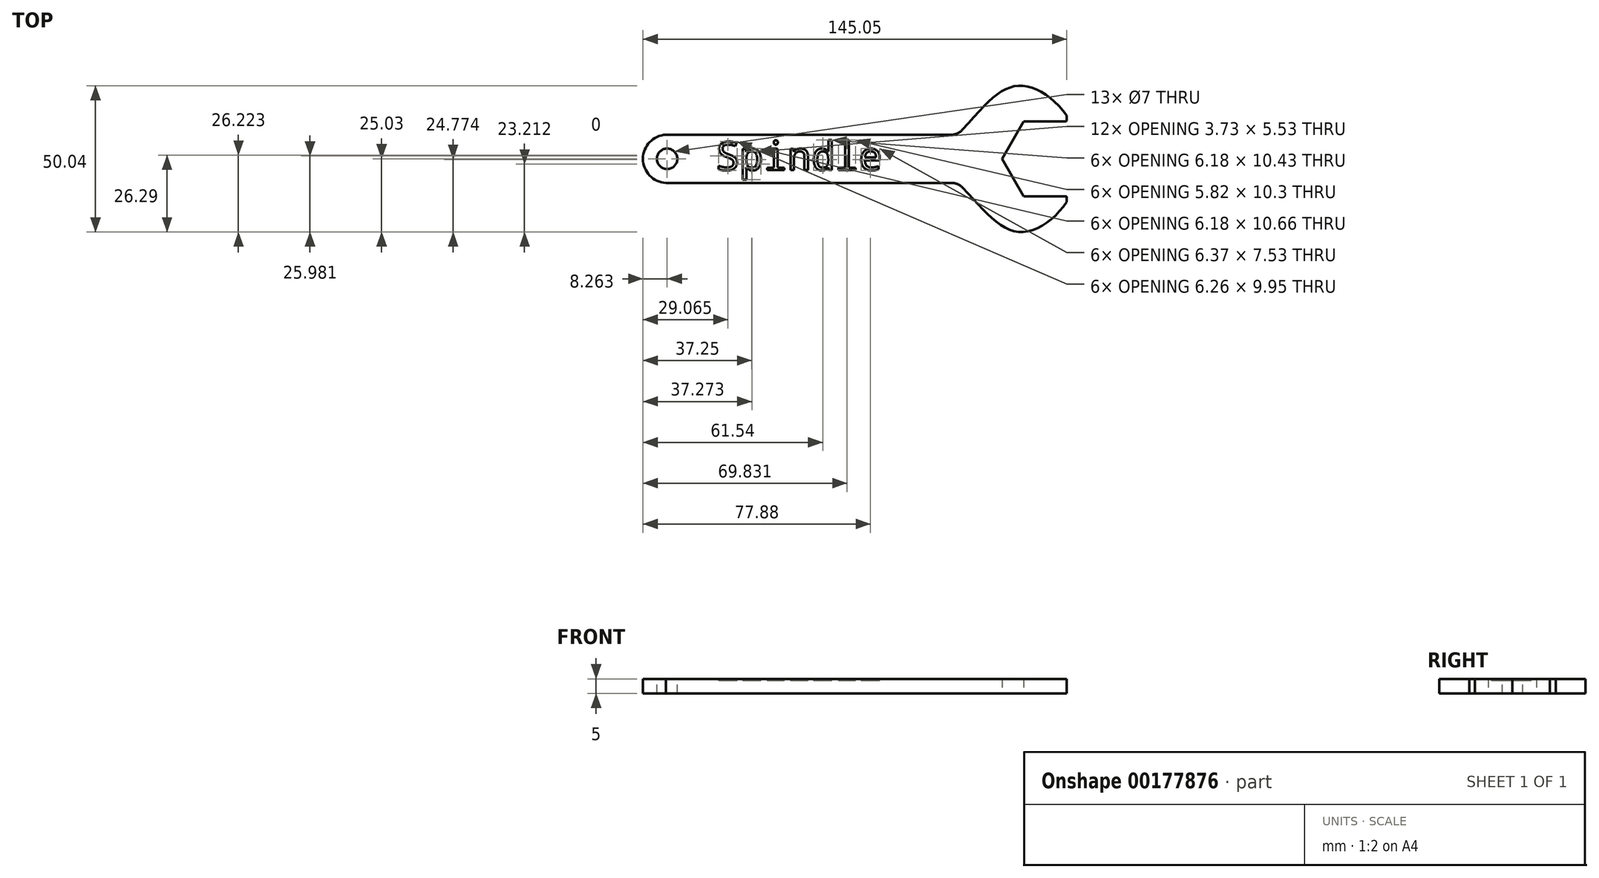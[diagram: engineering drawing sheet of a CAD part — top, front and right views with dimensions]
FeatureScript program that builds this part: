
annotation { "Feature Type Name" : "Feature", "Feature Type Description" : "" }
export const myFeature = defineFeature(function(context is Context, id is Id, definition is map)
    precondition{}
    {
        {
            var Q0;
            Q0=qCreatedBy(makeId("Top.planeOp"),FACE);
            var sketch = newSketch(context, id + "F0", { "sketchPlane" : qUnion([Q0])});
            skCircle(sketch, "E0.cCircle", {"center": v(0, 0) * mm, "radius": 12.8 * mm, "construction": true});
            skLineSegment(sketch, "E0.0", {"start": v(-7.4, 12.8) * mm, "end": v(7.4, 12.8) * mm});
            skLineSegment(sketch, "E0.1", {"start": v(7.4, 12.8) * mm, "end": v(14.78, 0) * mm});
            skLineSegment(sketch, "E0.2", {"start": v(14.78, 0) * mm, "end": v(7.4, -12.8) * mm});
            skLineSegment(sketch, "E0.3", {"start": v(7.4, -12.8) * mm, "end": v(-7.4, -12.8) * mm});
            skLineSegment(sketch, "E0.4", {"start": v(-7.4, -12.8) * mm, "end": v(-14.78, 0) * mm});
            skLineSegment(sketch, "E0.5", {"start": v(-14.78, 0) * mm, "end": v(-7.4, 12.8) * mm});
            skPoint(sketch, "E0.0.midPoint", {"position": v(0, 12.8) * mm});
            skLineSegment(sketch, "E1.bottom", {"start": v(-29.78, 8.25) * mm, "end": v(-29.78, 8.25) * mm});
            skLineSegment(sketch, "E1.top", {"start": v(-29.78, -8.25) * mm, "end": v(-29.78, -8.25) * mm});
            skLineSegment(sketch, "E1.left", {"start": v(-29.78, 8.25) * mm, "end": v(-29.78, -8.25) * mm});
            skLineSegment(sketch, "E1.right", {"start": v(-29.78, 8.25) * mm, "end": v(-29.78, -8.25) * mm});
            skLineSegment(sketch, "E2.bottom", {"start": v(-129.78, 8.25) * mm, "end": v(-29.78, 8.25) * mm});
            skLineSegment(sketch, "E2.top", {"start": v(-129.78, -8.25) * mm, "end": v(-29.78, -8.25) * mm});
            skLineSegment(sketch, "E2.left", {"start": v(-129.78, 8.25) * mm, "end": v(-129.78, -8.25) * mm});
            skCircle(sketch, "E3", {"center": v(-129.4, 0) * mm, "radius": 8.26 * mm});
            skPoint(sketch, "E3.third.point", {"position": v(-136.59, 4.06) * mm});
            skLineSegment(sketch, "E4", {"start": v(7.4, -12.8) * mm, "end": v(7.4, -14.8) * mm});
            skLineSegment(sketch, "E5", {"start": v(7.4, 12.8) * mm, "end": v(7.4, 14.8) * mm});
            skFitSpline(sketch, "E6", {"points": [v(7.4, 14.8) * mm, v(-9, 25) * mm, v(-29.78, 8.25) * mm], "startDerivative": vector(-30.28, 42.36) * mm, "endDerivative": vector(-51.1, -58.48) * mm});
            skFitSpline(sketch, "E7", {"points": [v(7.4, -14.8) * mm, v(-9, -25) * mm, v(-29.78, -8.25) * mm], "startDerivative": vector(-27.5, -40.28) * mm, "endDerivative": vector(-46.01, 49.34) * mm});
            skSolve(sketch);
        }
        {
            var Q0;
            {var subQ3=sQuery(id+"F0.wireOp",EDGE,"E2.bottom");Q0=makeQuery(id+"F0.imprint","IMPRINT",FACE,{"disambiguationData":[TD([[makeQuery(id+"F0.imprint","IMPRINT",EDGE,{"derivedFrom":subQ3}),-1.0]])]});}
            var Q1;
            {var subQ0=sQuery(id+"F0.wireOp",EDGE,"E2.left");Q1=makeQuery(id+"F0.imprint","IMPRINT",FACE,{"disambiguationData":[TD([[makeQuery(id+"F0.imprint","IMPRINT",EDGE,{"derivedFrom":subQ0}),1.0]])]});}
            var Q2;
            {var subQ0=sQuery(id+"F0.wireOp",EDGE,"E2.left");Q2=makeQuery(id+"F0.imprint","IMPRINT",FACE,{"disambiguationData":[TD([[makeQuery(id+"F0.imprint","IMPRINT",EDGE,{"derivedFrom":subQ0}),-1.0]])]});}
            var Q3;
            Q3=makeQuery(id+"F0.imprint","IMPRINT",FACE,{"disambiguationData":[TD([[makeQuery(id+"F0.imprint","IMPRINT",EDGE,{"derivedFrom":sQuery(id+"F0.wireOp",EDGE,"E0.0")}),1.0]])]});
            extrude(context, id + "F1", {"entities" : qUnion([Q0, Q1, Q2, Q3]), "depth" : 5 * mm});
        }
        {
            var Q0;
            Q0=makeQuery(id+"F1.opExtrude","CAP_FACE",FACE,{"disambiguationData":[OSD([sQuery(id+"F0.wireOp",EDGE,"E0.0"),sQuery(id+"F0.wireOp",EDGE,"E0.3"),sQuery(id+"F0.wireOp",EDGE,"E0.4"),sQuery(id+"F0.wireOp",EDGE,"E0.5"),sQuery(id+"F0.wireOp",EDGE,"8e9e9b65-ac2f-468e-a00c-45cfab599eec"),sQuery(id+"F0.wireOp",EDGE,"dbf11928-1581-4c0f-8f04-2778a1c86a44"),sQuery(id+"F0.wireOp",EDGE,"E2.bottom"),sQuery(id+"F0.wireOp",EDGE,"E2.top"),sQuery(id+"F0.wireOp",EDGE,"E1.left"),sQuery(id+"F0.wireOp",EDGE,"E3")])],"isStart":false});
            var sketch = newSketch(context, id + "F2", { "sketchPlane" : qUnion([Q0])});
            skCircle(sketch, "E8", {"center": v(-129.4, 0) * mm, "radius": 3.5 * mm});
            skSolve(sketch);
        }
        {
            var Q0;
            Q0=makeQuery(id+"F2.imprint","IMPRINT",FACE,{"disambiguationData":[TD([[makeQuery(id+"F2.imprint","IMPRINT",EDGE,{"derivedFrom":sQuery(id+"F2.wireOp",EDGE,"E8")}),1.0]])]});
            extrude(context, id + "F3", {"entities" : qUnion([Q0]), "operationType" : NewBodyOperationType.REMOVE, "oppositeDirection" : true, "depth" : 25 * mm});
        }
        {
            var Q0;
            Q0=makeQuery(id+"F1.opExtrude","CAP_FACE",FACE,{"disambiguationData":[OSD([sQuery(id+"F0.wireOp",EDGE,"E0.0"),sQuery(id+"F0.wireOp",EDGE,"E0.3"),sQuery(id+"F0.wireOp",EDGE,"E0.4"),sQuery(id+"F0.wireOp",EDGE,"E0.5"),sQuery(id+"F0.wireOp",EDGE,"8e9e9b65-ac2f-468e-a00c-45cfab599eec"),sQuery(id+"F0.wireOp",EDGE,"dbf11928-1581-4c0f-8f04-2778a1c86a44"),sQuery(id+"F0.wireOp",EDGE,"E2.bottom"),sQuery(id+"F0.wireOp",EDGE,"E2.top"),sQuery(id+"F0.wireOp",EDGE,"E1.left"),sQuery(id+"F0.wireOp",EDGE,"E3")])],"isStart":false});
            var sketch = newSketch(context, id + "F4", { "sketchPlane" : qUnion([Q0])});
            skText(sketch, "E9", { "text": "Spindle", "fontName": "DroidSansMono.ttf"});
            const initialGuessF4  = {"E9": [-0.11266, -0.00389, 1, 0, 0.00976]};
            skSetInitialGuess(sketch, initialGuessF4);
            skSolve(sketch);
        }
        {
            var Q0;
            Q0=qSketchRegion(id+"F4",true);
            extrude(context, id + "F5", {"entities" : qUnion([Q0]), "operationType" : NewBodyOperationType.REMOVE, "oppositeDirection" : true, "depth" : .5 * mm});
        }
        {
            var Q0;
            Q0=makeQuery(id+"F1.opExtrude","SWEPT_EDGE",EDGE,{"disambiguationData":[OSD([sQuery(id+"F0.wireOp",EDGE,"8e9e9b65-ac2f-468e-a00c-45cfab599eec"),sQuery(id+"F0.wireOp",EDGE,"E2.bottom"),sQuery(id+"F0.wireOp",EDGE,"E1.left")])]});
            var Q1;
            Q1=makeQuery(id+"F1.opExtrude","SWEPT_EDGE",EDGE,{"disambiguationData":[OSD([sQuery(id+"F0.wireOp",EDGE,"dbf11928-1581-4c0f-8f04-2778a1c86a44"),sQuery(id+"F0.wireOp",EDGE,"E2.top"),sQuery(id+"F0.wireOp",EDGE,"E1.left")])]});
            fillet(context, id + "F6", {"entities" : qUnion([Q0, Q1]), "radius" : 5 * mm, "tangentPropagation" : true, "allowEdgeOverflow" : false});
        }
        {
            var Q0;
            Q0=makeQuery(id+"F1.opExtrude","SWEPT_EDGE",EDGE,{"disambiguationData":[OSD([sQuery(id+"F0.wireOp",EDGE,"E0.0"),sQuery(id+"F0.wireOp",EDGE,"E0.1"),sQuery(id+"F0.wireOp",EDGE,"8e9e9b65-ac2f-468e-a00c-45cfab599eec")])]});
            var Q1;
            Q1=makeQuery(id+"F1.opExtrude","SWEPT_EDGE",EDGE,{"disambiguationData":[OSD([sQuery(id+"F0.wireOp",EDGE,"E0.2"),sQuery(id+"F0.wireOp",EDGE,"E0.3"),sQuery(id+"F0.wireOp",EDGE,"dbf11928-1581-4c0f-8f04-2778a1c86a44")])]});
            fillet(context, id + "F7", {"entities" : qUnion([Q0, Q1]), "radius" : .5 * mm, "tangentPropagation" : true, "allowEdgeOverflow" : false});
        }
    });
